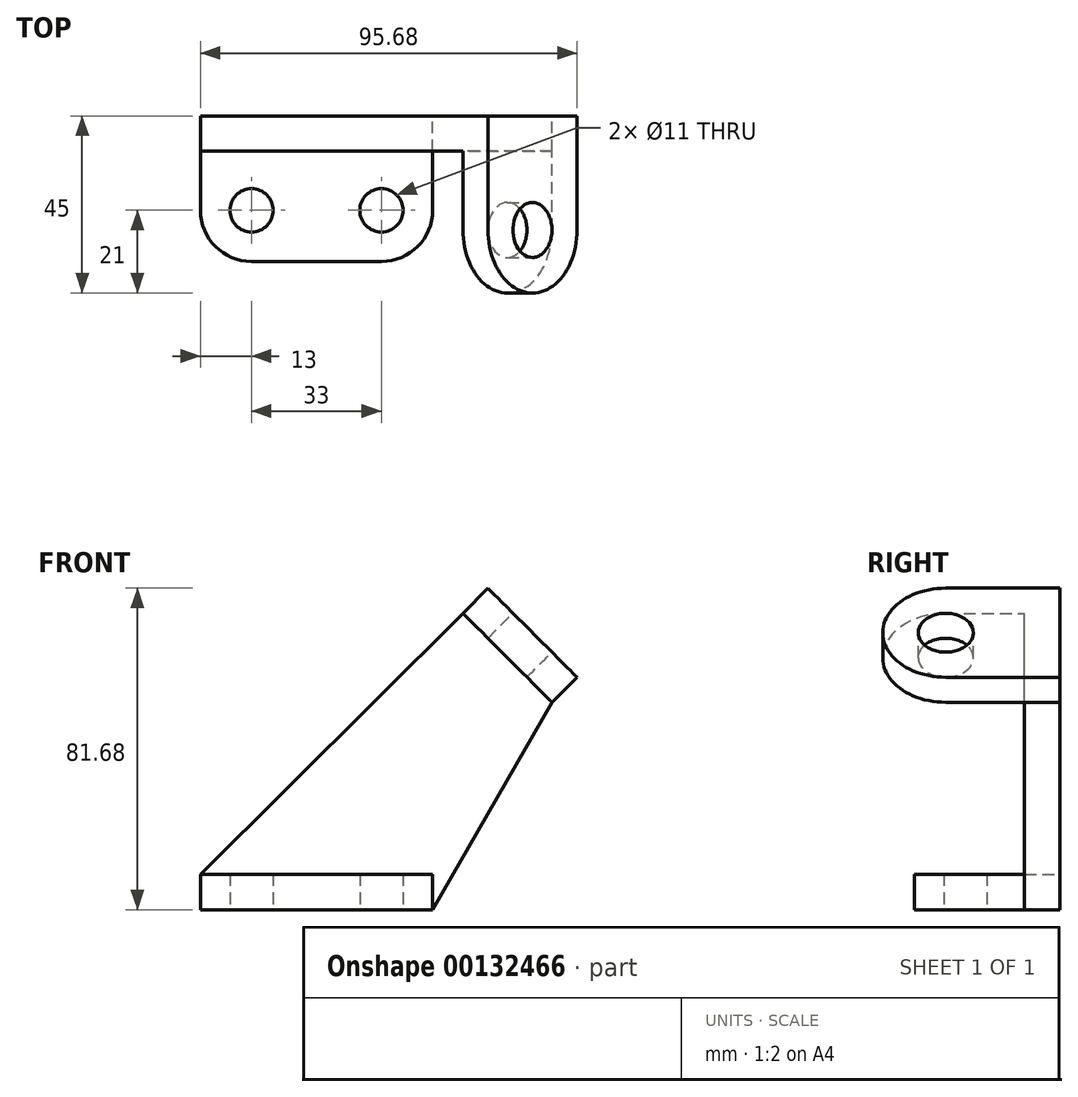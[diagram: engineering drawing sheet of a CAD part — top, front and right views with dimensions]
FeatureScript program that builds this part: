
annotation { "Feature Type Name" : "Feature", "Feature Type Description" : "" }
export const myFeature = defineFeature(function(context is Context, id is Id, definition is map)
    precondition{}
    {
        {
            var Q0;
            Q0=qCreatedBy(makeId("Top.planeOp"),FACE);
            var sketch = newSketch(context, id + "F0", { "sketchPlane" : qUnion([Q0])});
            skCircle(sketch, "E0", {"center": v(0, 0) * mm, "radius": 5.5 * mm});
            skLineSegment(sketch, "E1", {"start": v(0, 0) * mm, "end": v(33, 0) * mm});
            skCircle(sketch, "E2", {"center": v(33, 0) * mm, "radius": 5.5 * mm});
            skLineSegment(sketch, "E3", {"start": v(0, 0) * mm, "end": v(-13, 0) * mm, "construction": true});
            skLineSegment(sketch, "E4", {"start": v(0, 0) * mm, "end": v(0, -13) * mm, "construction": true});
            skLineSegment(sketch, "E5", {"start": v(46, 0) * mm, "end": v(33, 0) * mm, "construction": true});
            skLineSegment(sketch, "E6", {"start": v(33, 0) * mm, "end": v(33, -13) * mm, "construction": true});
            skArc(sketch, "E7", {"start": v(-13, 0) * mm, "mid": v(-9.2, -9.2) * mm, "end": v(0, -13) * mm});
            skArc(sketch, "E8", {"start": v(33, -13) * mm, "mid": v(42.2, -9.2) * mm, "end": v(46, 0) * mm});
            skLineSegment(sketch, "E9", {"start": v(0, -13) * mm, "end": v(33, -13) * mm});
            skLineSegment(sketch, "E10", {"start": v(-13, 0) * mm, "end": v(-13, 24) * mm});
            skLineSegment(sketch, "E11", {"start": v(46, 0) * mm, "end": v(46, 24) * mm});
            skLineSegment(sketch, "E12", {"start": v(46, 24) * mm, "end": v(-13, 24) * mm});
            skSolve(sketch);
        }
        {
            var Q0;
            Q0=makeQuery(id+"F0.imprint","IMPRINT",FACE,{"disambiguationData":[TD([[makeQuery(id+"F0.imprint","IMPRINT",EDGE,{"derivedFrom":sQuery(id+"F0.wireOp",EDGE,"E0")}),-1.0]])]});
            extrude(context, id + "F1", {"entities" : qUnion([Q0]), "depth" : 9 * mm});
        }
        {
            var Q0;
            Q0=makeQuery(id+"F1.opExtrude","SWEPT_FACE",FACE,{"disambiguationData":[OSD([sQuery(id+"F0.wireOp",EDGE,"E12")])]});
            var sketch = newSketch(context, id + "F2", { "sketchPlane" : qUnion([Q0])});
            skLineSegment(sketch, "E13", {"start": v(-46, 0) * mm, "end": v(-65, 0) * mm, "construction": true});
            skLineSegment(sketch, "E14", {"start": v(-65, 0) * mm, "end": v(-65, 64) * mm, "construction": true});
            skLineSegment(sketch, "E15", {"start": v(-65, 64) * mm, "end": v(-53.69, 75.31) * mm});
            skLineSegment(sketch, "E16", {"start": v(-65, 64) * mm, "end": v(-76.31, 52.69) * mm});
            skLineSegment(sketch, "E17", {"start": v(-76.31, 52.69) * mm, "end": v(-82.68, 59.05) * mm});
            skLineSegment(sketch, "E18", {"start": v(-82.68, 59.05) * mm, "end": v(-60.05, 81.68) * mm});
            skLineSegment(sketch, "E19", {"start": v(-60.05, 81.68) * mm, "end": v(-53.69, 75.31) * mm});
            skSolve(sketch);
        }
        {
            var Q0;
            {var subQ0=sQuery(id+"F0.wireOp",EDGE,"E12");Q0=makeQuery(id+"F2.imprint","IMPRINT",FACE,{"disambiguationData":[TD([[makeQuery(id+"F2.imprint","IMPRINT",EDGE,{"derivedFrom":makeQuery(id+"F1.opExtrude","CAP_EDGE",EDGE,{"disambiguationData":[OSD([subQ0])],"isStart":true})}),1.0]])]});}
            var sketch = newSketch(context, id + "F3", { "sketchPlane" : qUnion([Q0])});
            skLineSegment(sketch, "E20.0.0", {"start": v(-76.31, 52.69) * mm, "end": v(-65, 64) * mm});
            skLineSegment(sketch, "E20.0.1", {"start": v(-65, 64) * mm, "end": v(-53.69, 75.31) * mm});
            skLineSegment(sketch, "E20.0.2", {"start": v(-53.69, 75.31) * mm, "end": v(-60.05, 81.68) * mm});
            skLineSegment(sketch, "E20.0.3", {"start": v(-60.05, 81.68) * mm, "end": v(-82.68, 59.05) * mm});
            skLineSegment(sketch, "E20.0.4", {"start": v(-82.68, 59.05) * mm, "end": v(-76.31, 52.69) * mm});
            skLineSegment(sketch, "E21.0.0", {"start": v(-46, 9) * mm, "end": v(-46, 0) * mm});
            skLineSegment(sketch, "E21.0.1", {"start": v(-46, 0) * mm, "end": v(13, 0) * mm});
            skLineSegment(sketch, "E21.0.2", {"start": v(13, 0) * mm, "end": v(13, 9) * mm});
            skLineSegment(sketch, "E21.0.3", {"start": v(13, 9) * mm, "end": v(-46, 9) * mm});
            skLineSegment(sketch, "E22", {"start": v(13, 9) * mm, "end": v(-53.69, 75.31) * mm});
            skLineSegment(sketch, "E23", {"start": v(-46, 0) * mm, "end": v(-76.31, 52.69) * mm});
            skSolve(sketch);
        }
        {
            var Q0;
            Q0=makeQuery(id+"F3.imprint","IMPRINT",FACE,{"disambiguationData":[TD([[makeQuery(id+"F3.imprint","IMPRINT",EDGE,{"derivedFrom":sQuery(id+"F3.wireOp",EDGE,"E20.0.0")}),-1.0]])]});
            extrude(context, id + "F4", {"entities" : qUnion([Q0]), "operationType" : NewBodyOperationType.ADD, "oppositeDirection" : true, "depth" : 9 * mm});
        }
        {
            var Q0;
            Q0=makeQuery(id+"F2.imprint","IMPRINT",FACE,{"disambiguationData":[TD([[makeQuery(id+"F2.imprint","IMPRINT",EDGE,{"derivedFrom":sQuery(id+"F2.wireOp",EDGE,"E15")}),1.0]])]});
            extrude(context, id + "F5", {"entities" : qUnion([Q0]), "operationType" : NewBodyOperationType.ADD, "oppositeDirection" : true, "depth" : 29 * mm});
        }
        {
            var Q0;
            Q0=makeQuery(id+"F5.opExtrude","SWEPT_FACE",FACE,{"disambiguationData":[OSD([sQuery(id+"F2.wireOp",EDGE,"E18")])]});
            var sketch = newSketch(context, id + "F6", { "sketchPlane" : qUnion([Q0])});
            skArc(sketch, "E24", {"start": v(-5, 15.3) * mm, "mid": v(-21, -0.7) * mm, "end": v(-5, -16.7) * mm});
            skCircle(sketch, "E25", {"center": v(-5, -0.7) * mm, "radius": 7 * mm});
            skSolve(sketch);
        }
        {
            var Q0;
            {var subQ0=sQuery(id+"F6.wireOp",EDGE,"E25");var subQ1=makeQuery(id+"F5.opExtrude","CAP_EDGE",EDGE,{"disambiguationData":[OSD([sQuery(id+"F2.wireOp",EDGE,"E18")])],"isStart":false});var subQ2=makeQuery(id+"F6.imprint","INTERSECT",VERTEX,{"disambiguationData":[OD(0.0)],"derivedFrom":[subQ1,subQ0]});Q0=makeQuery(id+"F6.imprint","IMPRINT",FACE,{"disambiguationData":[TD([[makeQuery(id+"F6.imprint","IMPRINT",EDGE,{"disambiguationData":[TD([[subQ2,-1.0]])],"derivedFrom":subQ0}),1.0]])]});}
            extrude(context, id + "F7", {"entities" : qUnion([Q0]), "operationType" : NewBodyOperationType.REMOVE, "oppositeDirection" : true, "depth" : 9 * mm});
        }
        {
            var Q0;
            {var subQ0=sQuery(id+"F6.wireOp",EDGE,"E24");Q0=makeQuery(id+"F6.imprint","IMPRINT",FACE,{"disambiguationData":[TD([[makeQuery(id+"F6.imprint","IMPRINT",EDGE,{"derivedFrom":subQ0}),1.0]])]});}
            extrude(context, id + "F8", {"entities" : qUnion([Q0]), "operationType" : NewBodyOperationType.ADD, "oppositeDirection" : true, "depth" : 9 * mm});
        }
    });
